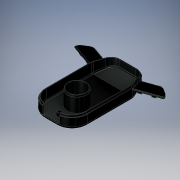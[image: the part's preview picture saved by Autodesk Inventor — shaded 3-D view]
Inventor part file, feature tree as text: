
AUTODESK INVENTOR PART (.ipt)
format: ipt  version: 2019 (Build 230136000, 136)  size: 603,136 bytes
history: native  units: mm
features: sketch x18, extrude x13, plane x7, fillet x6, other x5, projected_geometry x5, mirror x3, loft x1, shell x1, split x1, sweep x1, surface_op x1
ambient origin geometry x8: Origin, YZ Plane, XZ Plane, XY Plane, X Axis, Y Axis, Z Axis, Center Point
bodies: Body1 (feature_tree), Body2 (feature_tree), Body3 (feature_tree), Body4 (feature_tree)
feature tree (62):
  other  "ROV Hull - Bottom"
  extrude  "Extrusion1"  Depth=90.0mm
  plane  "Work Plane2"
  loft  "Loft2"
  fillet  "Fillet1"  Radius=180.0mm
  fillet  "Fillet2"  [1 undecoded]
  fillet  "Fillet3"  [1 undecoded]
  fillet  "Fillet4"  Radius=60.0mm
  shell  "Shell2"  Thickness=50.0mm
  sketch  "Sketch6"  dims[d33=50.0mm d34=16.0mm]
  extrude  "Extrusion2"  Depth=16.0mm
  other  "Lip1"
  other  "Lip2"
  sketch  "Sketch9"  dims[d35=10.0mm d36=360.0mm]
  split  "Split1"
  sketch  "Sketch10"  dims[d47=90.0mm d48=0.0mm]
  extrude  "Extrusion5"  Depth=10.0mm
  extrude  "Extrusion6"  Depth=10.0mm TaperAngle=0.0deg
  sketch  "Sketch12"  dims[d62=10.0mm d63=4.0mm d64=0.0mm d65=0.0mm d66=0.349066mm d67=0.0mm d77=30.0mm d78=0.0mm]
  plane  "Work Plane3"
  mirror  "Mirror1"
  plane  "Work Plane4"
  sketch  "Sketch13"  dims[d83=5.0mm d84=140.0mm d85=0.0mm]
  plane  "Work Plane5"
  extrude  "Extrusion12"  Depth=140.0mm TaperAngle=0.0deg
  plane  "Work Plane6"
  plane  "Work Plane7"
  extrude  "Extrusion15"  Depth=70.0mm
  extrude  "Extrusion16"  [1 undecoded]
  extrude  "Extrusion18"  Depth=10.0mm TaperAngle=0.0deg
  extrude  "Extrusion19"  Depth=344.0mm
  fillet  "Fillet8"  Radius=25.0mm
  mirror  "Mirror5"
  extrude  "Extrusion20"  Depth=5.0mm
  plane  "Work Plane8"
  extrude  "Extrusion22"  Depth=5.0mm TaperAngle=0.0deg
  fillet  "Fillet10"  [1 undecoded]
  mirror  "Mirror6"
  extrude  "Extrusion23"  Depth=20.0mm TaperAngle=0.0deg
  extrude  "Extrusion24"  Depth=40.0mm TaperAngle=0.0deg
  sweep  "Sweep1"
  sketch  "Sketch1"  dims[d8=250.0mm d10=90.0mm]
  sketch  "Sketch5"  dims[d11=60.0mm d12=0.0mm d22=100.0mm d24=180.0mm d26=0.0mm d27=90.0deg d28=0.0mm d29=90.0deg d30=60.0mm d32=50.0mm]
  other  "Edges1"
  projected_geometry  "Projected Loop9"
  sketch  "Sketch11"  dims[d55=10.0mm d56=4.0mm d57=0.0mm d58=0.0mm d59=0.349066mm d60=0.0mm]
  projected_geometry  "Projected Loop12"
  sketch  "Sketch18"  dims[d94=-125.0mm d95=70.0mm]
  other  "Srf3"
  sketch  "Sketch20"  dims[d96=39.0mm d97=-405.0mm]
  projected_geometry  "Projected Loop19"
  projected_geometry  "Projected Loop20"
  sketch  "Sketch22"  dims[d123=5.0mm d124=10.0mm d125=0.0mm]
  sketch  "Sketch23"  dims[d133=0.0mm d135=344.0mm d139=25.0mm]
  sketch  "Sketch24"  dims[d140=18.0mm d143=5.0mm]
  projected_geometry  "Projected Loop25"
  sketch  "Sketch26"  dims[d144=5.0mm d162=2.5mm d173=5.0mm d174=0.0mm d175=-5.0mm]
  sketch  "Sketch27"  dims[d176=60.0mm d177=0.0mm d178=20.0mm d179=0.0mm]
  sketch  "Sketch28"  dims[d187=57.0mm d188=0.0mm d191=40.0mm d192=0.0mm]
  sketch  "Sketch29"  dims[d193=2.0mm d194=12.0mm]
  sketch  "Sketch30"  dims[d195=8.0mm d196=65.0mm d197=0.0mm d198=17.0mm d206=4.0mm d207=0.0mm d208=3.0mm d212=11.0mm d213=0.0mm d214=100.0mm d215=12.0mm d216=0.0mm d217=90.0mm d218=5.0mm d220=13.0mm d221=0.0mm d222=0.0mm d226=10.0mm]
  surface_op  "Boundary Patch3"
note: 4 required parameter values undecoded (feature->parameter linkage not recoverable at this tier; creation-order binding heuristic only, values carry confidence <= 0.55)
